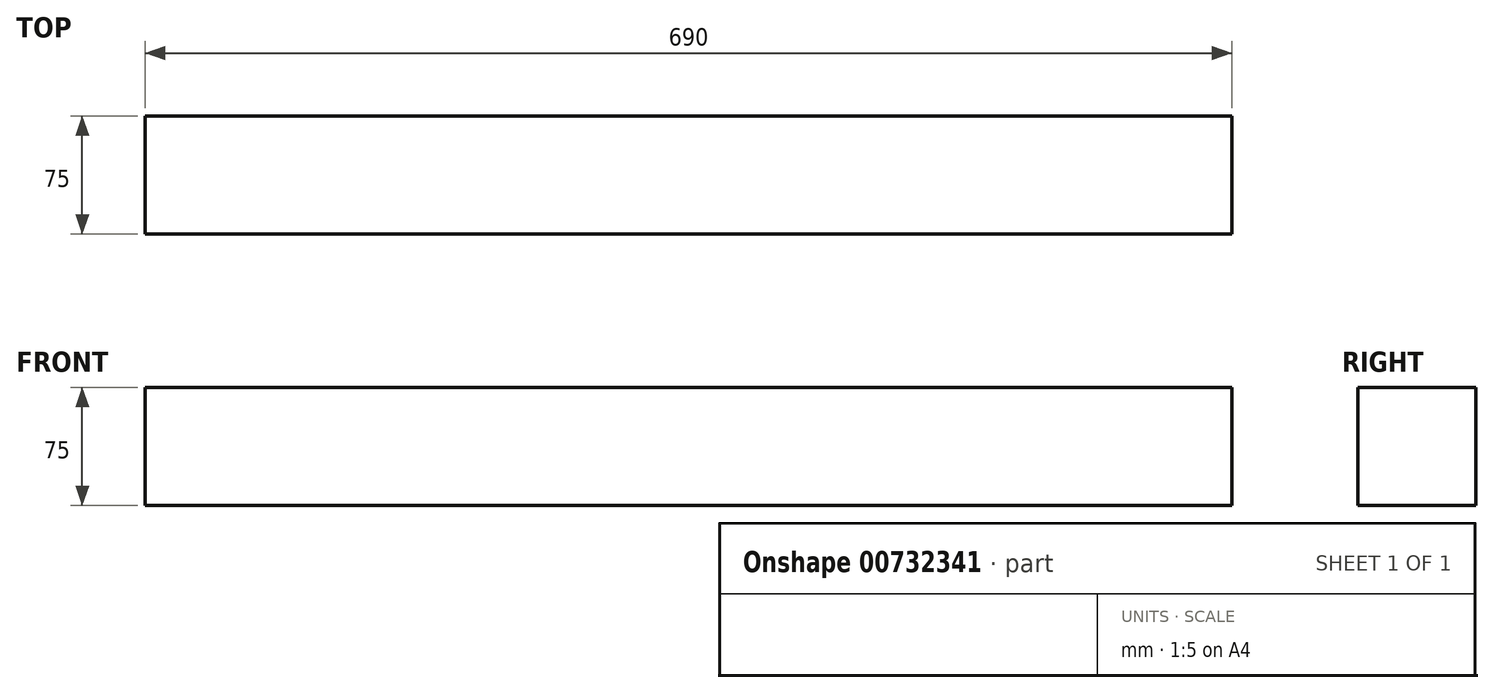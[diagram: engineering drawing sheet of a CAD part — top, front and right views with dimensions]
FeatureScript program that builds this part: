
annotation { "Feature Type Name" : "Feature", "Feature Type Description" : "" }
export const myFeature = defineFeature(function(context is Context, id is Id, definition is map)
    precondition{}
    {
        {
            var Q0;
            Q0=qCreatedBy(makeId("Top.planeOp"),FACE);
            var sketch = newSketch(context, id + "F0", { "sketchPlane" : qUnion([Q0])});
            skLineSegment(sketch, "E0.bottom", {"start": v(-348.6, 37.5) * mm, "end": v(341.4, 37.5) * mm});
            skLineSegment(sketch, "E0.top", {"start": v(-348.6, -37.5) * mm, "end": v(341.4, -37.5) * mm});
            skLineSegment(sketch, "E0.left", {"start": v(-348.6, 37.5) * mm, "end": v(-348.6, -37.5) * mm});
            skLineSegment(sketch, "E0.right", {"start": v(341.4, 37.5) * mm, "end": v(341.4, -37.5) * mm});
            skPoint(sketch, "E0.middle", {"position": v(-3.6, 0) * mm});
            skSolve(sketch);
        }
        {
            var Q0;
            Q0=makeQuery(id+"F0.imprint","IMPRINT",FACE,{"disambiguationData":[TD([[makeQuery(id+"F0.imprint","IMPRINT",EDGE,{"derivedFrom":sQuery(id+"F0.wireOp",EDGE,"E0.bottom")}),-1.0]])]});
            extrude(context, id + "F1", {"entities" : qUnion([Q0]), "depth" : 75 * mm, "offsetDistance" : 25 * mm});
        }
    });
